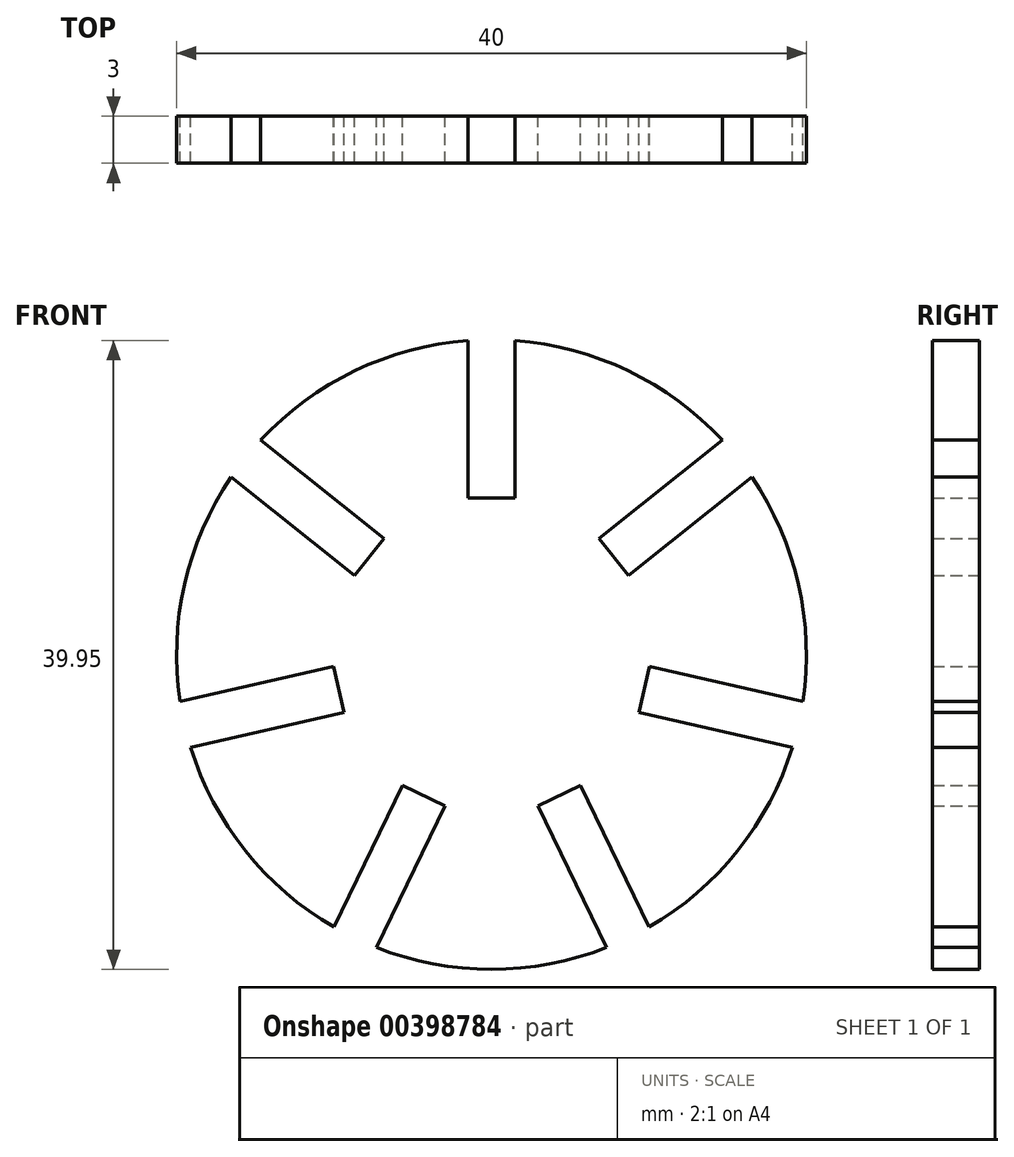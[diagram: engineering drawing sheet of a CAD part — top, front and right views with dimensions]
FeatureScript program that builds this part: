
annotation { "Feature Type Name" : "Feature", "Feature Type Description" : "" }
export const myFeature = defineFeature(function(context is Context, id is Id, definition is map)
    precondition{}
    {
        {
            var Q0;
            Q0=qCreatedBy(makeId("Front.planeOp"),FACE);
            var sketch = newSketch(context, id + "F0", { "sketchPlane" : qUnion([Q0])});
            skPoint(sketch, "E0", {"position": v(-2.51, 13.45) * mm});
            skPoint(sketch, "E1", {"position": v(0.49, 13.45) * mm});
            skLineSegment(sketch, "E2", {"start": v(0.49, 3.45) * mm, "end": v(-2.51, 3.45) * mm});
            skLineSegment(sketch, "E3", {"start": v(-2.51, 3.45) * mm, "end": v(-2.51, 13.45) * mm});
            skLineSegment(sketch, "E4", {"start": v(0.49, 13.45) * mm, "end": v(0.49, 3.45) * mm});
            skArc(sketch, "E5", {"start": v(-2.51, 13.45) * mm, "mid": v(-9.69, 11.52) * mm, "end": v(-15.67, 7.11) * mm});
            skPoint(sketch, "E6.1.0", {"position": v(-17.54, 4.77) * mm});
            skLineSegment(sketch, "E6.1.1", {"start": v(-15.67, 7.11) * mm, "end": v(-7.85, 0.88) * mm});
            skLineSegment(sketch, "E6.1.2", {"start": v(-9.72, -1.47) * mm, "end": v(-17.54, 4.77) * mm});
            skPoint(sketch, "E6.1.3", {"position": v(-15.67, 7.11) * mm});
            skLineSegment(sketch, "E6.1.4", {"start": v(-7.85, 0.88) * mm, "end": v(-9.72, -1.47) * mm});
            skPoint(sketch, "E6.2.0", {"position": v(-20.12, -12.4) * mm});
            skLineSegment(sketch, "E6.2.1", {"start": v(-20.79, -9.47) * mm, "end": v(-11.04, -7.25) * mm});
            skLineSegment(sketch, "E6.2.2", {"start": v(-10.37, -10.17) * mm, "end": v(-20.12, -12.4) * mm});
            skPoint(sketch, "E6.2.3", {"position": v(-20.79, -9.47) * mm});
            skLineSegment(sketch, "E6.2.4", {"start": v(-11.04, -7.25) * mm, "end": v(-10.37, -10.17) * mm});
            skPoint(sketch, "E6.3.0", {"position": v(-8.31, -25.12) * mm});
            skLineSegment(sketch, "E6.3.1", {"start": v(-11.02, -23.81) * mm, "end": v(-6.68, -14.8) * mm});
            skLineSegment(sketch, "E6.3.2", {"start": v(-3.97, -16.1) * mm, "end": v(-8.31, -25.12) * mm});
            skPoint(sketch, "E6.3.3", {"position": v(-11.02, -23.81) * mm});
            skLineSegment(sketch, "E6.3.4", {"start": v(-6.68, -14.8) * mm, "end": v(-3.97, -16.1) * mm});
            skPoint(sketch, "E6.4.0", {"position": v(9, -23.81) * mm});
            skLineSegment(sketch, "E6.4.1", {"start": v(6.3, -25.12) * mm, "end": v(1.95, -16.1) * mm});
            skLineSegment(sketch, "E6.4.2", {"start": v(4.66, -14.8) * mm, "end": v(9, -23.81) * mm});
            skPoint(sketch, "E6.4.3", {"position": v(6.3, -25.12) * mm});
            skLineSegment(sketch, "E6.4.4", {"start": v(1.95, -16.1) * mm, "end": v(4.66, -14.8) * mm});
            skPoint(sketch, "E6.5.0", {"position": v(18.77, -9.47) * mm});
            skLineSegment(sketch, "E6.5.1", {"start": v(18.1, -12.4) * mm, "end": v(8.35, -10.17) * mm});
            skLineSegment(sketch, "E6.5.2", {"start": v(9.02, -7.25) * mm, "end": v(18.77, -9.47) * mm});
            skPoint(sketch, "E6.5.3", {"position": v(18.1, -12.4) * mm});
            skLineSegment(sketch, "E6.5.4", {"start": v(8.35, -10.17) * mm, "end": v(9.02, -7.25) * mm});
            skPoint(sketch, "E6.6.0", {"position": v(13.65, 7.11) * mm});
            skLineSegment(sketch, "E6.6.1", {"start": v(15.52, 4.77) * mm, "end": v(7.7, -1.47) * mm});
            skLineSegment(sketch, "E6.6.2", {"start": v(5.83, 0.88) * mm, "end": v(13.65, 7.11) * mm});
            skPoint(sketch, "E6.6.3", {"position": v(15.52, 4.77) * mm});
            skLineSegment(sketch, "E6.6.4", {"start": v(7.7, -1.47) * mm, "end": v(5.83, 0.88) * mm});
            skArc(sketch, "E7.trimOffspring", {"start": v(-17.54, 4.77) * mm, "mid": v(-20.5, -2.05) * mm, "end": v(-20.79, -9.47) * mm});
            skArc(sketch, "E8.trimOffspring", {"start": v(13.65, 7.11) * mm, "mid": v(7.67, 11.52) * mm, "end": v(0.49, 13.45) * mm});
            skArc(sketch, "E9.trimOffspring", {"start": v(18.77, -9.47) * mm, "mid": v(18.49, -2.05) * mm, "end": v(15.52, 4.77) * mm});
            skArc(sketch, "E10.trimOffspring", {"start": v(9, -23.81) * mm, "mid": v(14.63, -18.97) * mm, "end": v(18.1, -12.4) * mm});
            skArc(sketch, "E11.trimOffspring", {"start": v(-8.31, -25.12) * mm, "mid": v(-1.01, -26.5) * mm, "end": v(6.3, -25.12) * mm});
            skArc(sketch, "E12.trimOffspring", {"start": v(-20.12, -12.4) * mm, "mid": v(-16.65, -18.97) * mm, "end": v(-11.02, -23.81) * mm});
            skSolve(sketch);
        }
        {
            var Q0;
            Q0 = qSketchRegion(id + "F0", true);
            extrude(context, id + "F1", {"entities" : qUnion([Q0]), "depth" : 3 * mm});
        }
    });
